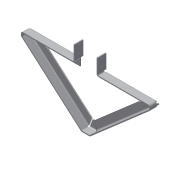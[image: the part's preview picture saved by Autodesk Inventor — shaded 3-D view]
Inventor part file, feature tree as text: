
AUTODESK INVENTOR PART (.ipt)
format: ipt  version: 2015 (Build 190159000, 159)  size: 358,912 bytes
history: native  units: in
note: dims shown in document units (in); Inventor stores cm internally (conversion verified against a paired STEP export)
features: sheet_metal_op x6, sketch x4, other x3, hole x2
ambient origin geometry x8: Origin, YZ Plane, XZ Plane, XY Plane, X Axis, Y Axis, Z Axis, Center Point
bodies: Solid1 (feature_tree)
feature tree (15):
  sheet_metal_op  "Contour Flange1"
  sheet_metal_op  "Flange1"
  hole  "Hole2"  [1 undecoded]
  hole  "Hole4"  [1 undecoded]
  sketch  "Sketch1"  dims[d0=0.5in d1=1.0in]
  other  "Plate1"
  sheet_metal_op  "Bend1"
  sheet_metal_op  "Corner1"
  sketch  "Sketch2"  dims[d4=0.12in d5=0.06in]
  other  "Plate2"
  sheet_metal_op  "Bend2"
  sheet_metal_op  "Corner2"
  sketch  "Sketch4"  dims[d6=0.24in]
  sketch  "Sketch6"  dims[d7=0.12in d8=1.0in d9=0.12in d10=0.12in d11=0.48in d12=0.12in d13=0.12in d14=0.12in d15=0.06in d16=0.24in d17=0.12in d18=1.0in d19=90.0deg d20=0.12in d21=0.48in d22=0.12in d23=0.12in d24=2.792in d33=1.75in d34=0.1in d35=0.75in d36=0.375in d37=0.25in d38=0.5635in d39=0.1in d40=0.0in d48=7.5in d49=14.0in d50=0.25in d51=0.75in d52=0.375in d53=0.25in d54=0.5635in d55=0.12in d56=0.0in]
  other  "Definition1"
note: 2 required parameter values undecoded (feature->parameter linkage not recoverable at this tier; creation-order binding heuristic only, values carry confidence <= 0.55)
